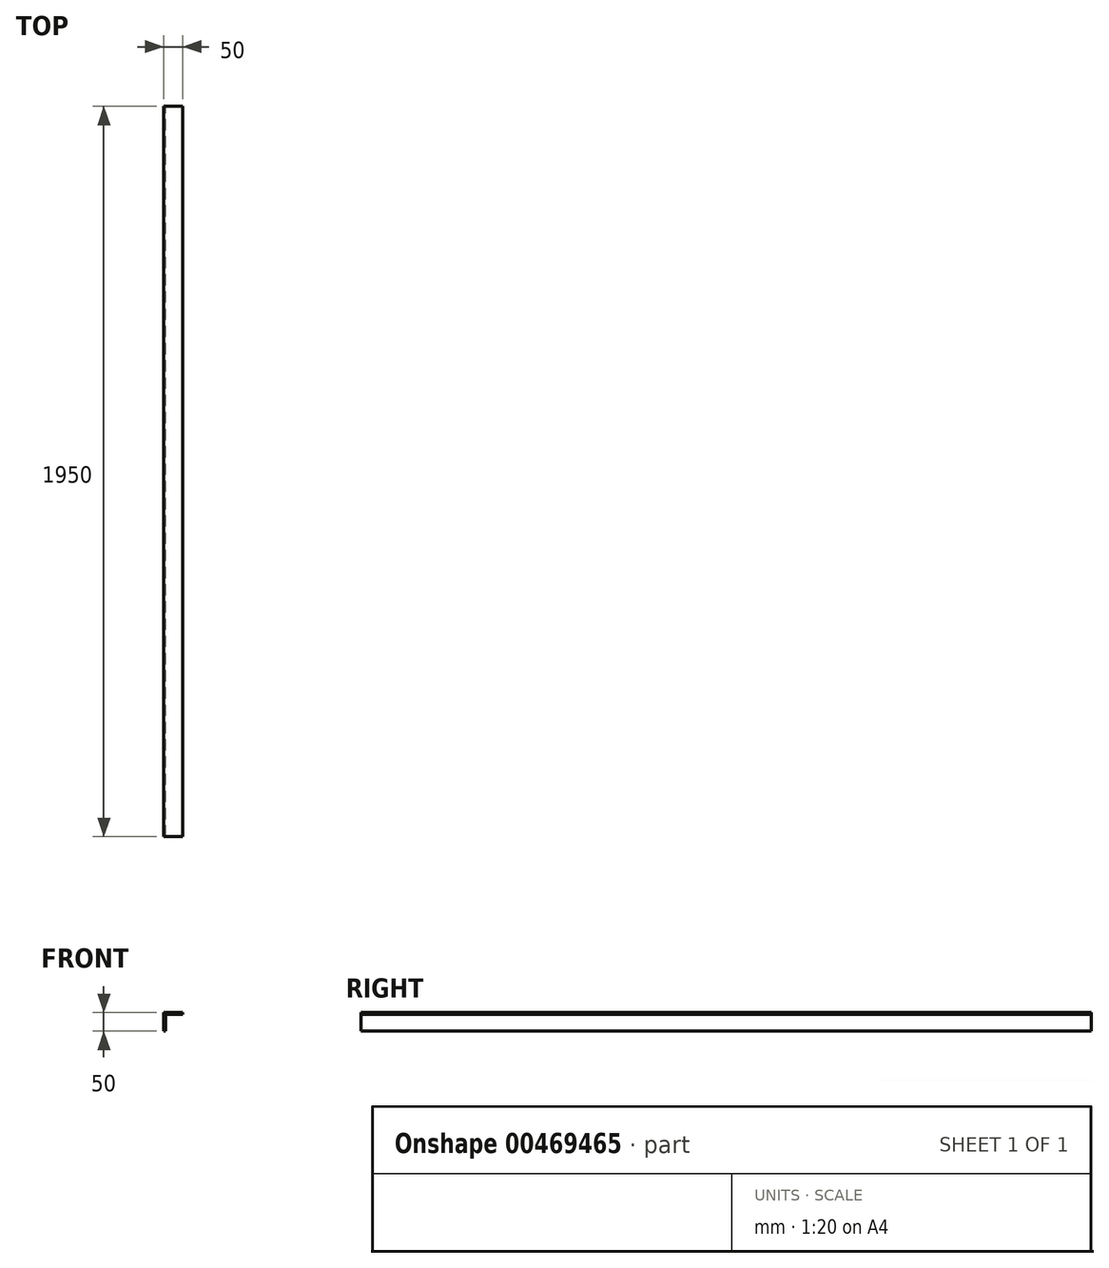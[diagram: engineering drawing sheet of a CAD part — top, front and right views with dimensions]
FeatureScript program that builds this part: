
annotation { "Feature Type Name" : "Feature", "Feature Type Description" : "" }
export const myFeature = defineFeature(function(context is Context, id is Id, definition is map)
    precondition{}
    {
        {
            var Q0;
            Q0=qCreatedBy(makeId("Front.planeOp"),FACE);
            var sketch = newSketch(context, id + "F0", { "sketchPlane" : qUnion([Q0])});
            skLineSegment(sketch, "E0", {"start": v(0, 0) * mm, "end": v(0, 50) * mm});
            skLineSegment(sketch, "E1", {"start": v(0, 50) * mm, "end": v(50, 50) * mm});
            skLineSegment(sketch, "E2", {"start": v(50, 50) * mm, "end": v(50, 45) * mm});
            skLineSegment(sketch, "E3", {"start": v(50, 45) * mm, "end": v(5, 45) * mm});
            skLineSegment(sketch, "E4", {"start": v(5, 45) * mm, "end": v(5, 0) * mm});
            skLineSegment(sketch, "E5", {"start": v(5, 0) * mm, "end": v(0, 0) * mm});
            skSolve(sketch);
        }
        {
            var Q0;
            Q0 = qSketchRegion(id + "F0", true);
            extrude(context, id + "F1", {"entities" : qUnion([Q0]), "depth" : 1950 * mm});
        }
    });
